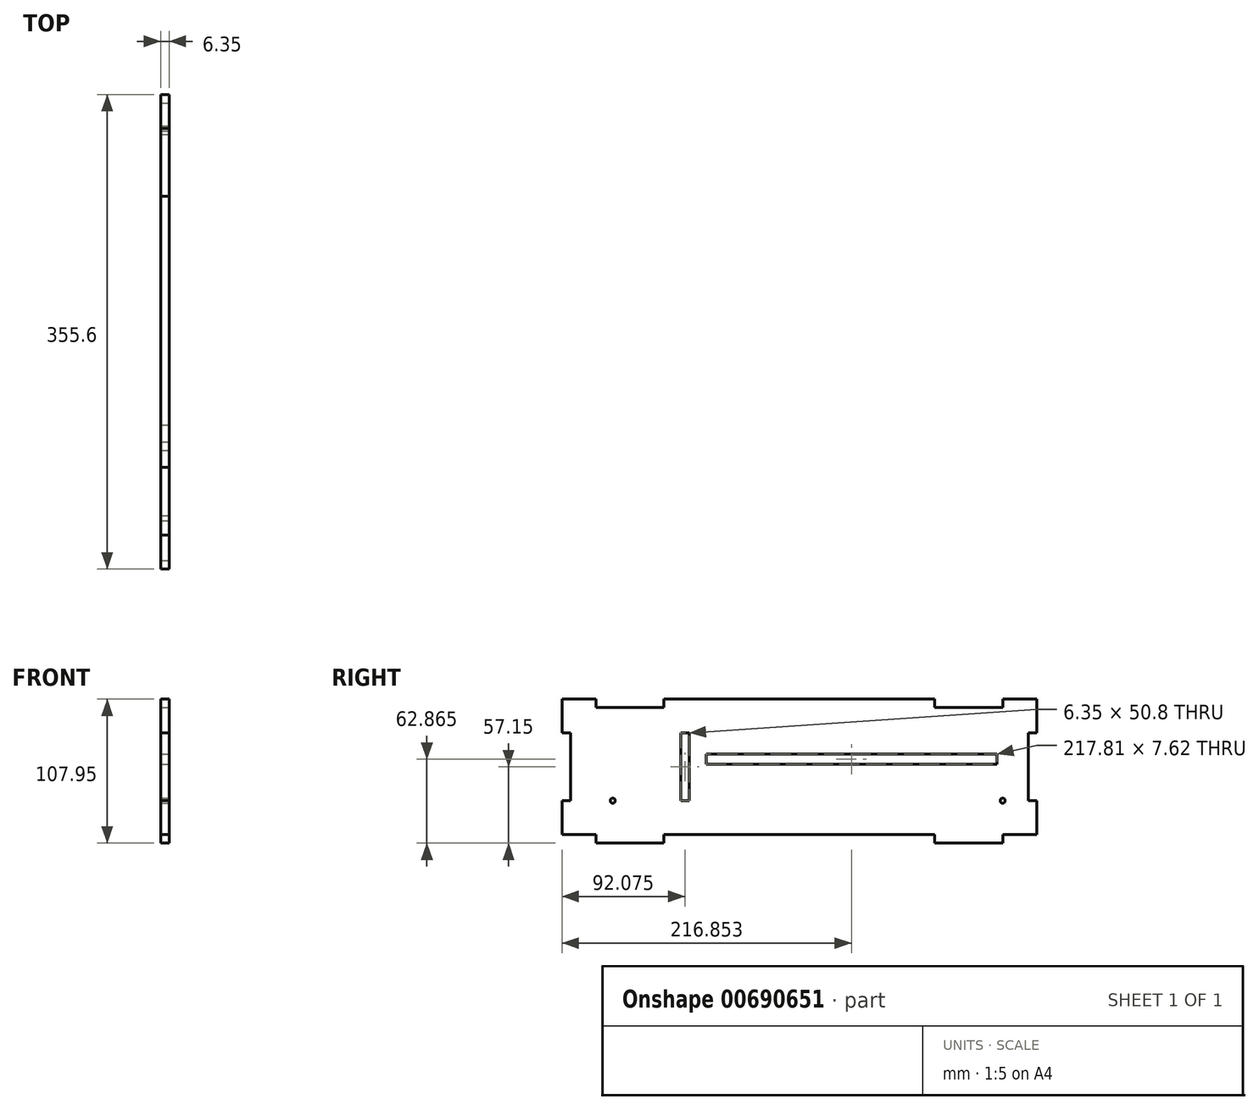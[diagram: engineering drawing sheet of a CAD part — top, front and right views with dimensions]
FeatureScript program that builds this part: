
annotation { "Feature Type Name" : "Feature", "Feature Type Description" : "" }
export const myFeature = defineFeature(function(context is Context, id is Id, definition is map)
    precondition{}
    {
        {
            var Q0;
            Q0=qCreatedBy(makeId("Right.planeOp"),FACE);
            var sketch = newSketch(context, id + "F0", { "sketchPlane" : qUnion([Q0])});
            skLineSegment(sketch, "E0.bottom", {"start": v(-177.8, 101.6) * mm, "end": v(177.8, 101.6) * mm});
            skLineSegment(sketch, "E0.top", {"start": v(-177.8, 0) * mm, "end": v(177.8, 0) * mm});
            skLineSegment(sketch, "E0.left", {"start": v(-177.8, 101.6) * mm, "end": v(-177.8, 0) * mm});
            skLineSegment(sketch, "E0.right", {"start": v(177.8, 101.6) * mm, "end": v(177.8, 0) * mm});
            skSolve(sketch);
        }
        {
            var Q0;
            Q0 = qSketchRegion(id + "F0", true);
            extrude(context, id + "F1", {"entities" : qUnion([Q0]), "depth" : 6.35 * mm, "offsetDistance" : 25.4 * mm});
        }
        {
            var Q0;
            Q0=makeQuery(id+"F1.opExtrude","CAP_FACE",FACE,{"disambiguationData":[OSD([sQuery(id+"F0.wireOp",EDGE,"E0.bottom"),sQuery(id+"F0.wireOp",EDGE,"E0.top"),sQuery(id+"F0.wireOp",EDGE,"E0.left"),sQuery(id+"F0.wireOp",EDGE,"E0.right")])],"isStart":false});
            var sketch = newSketch(context, id + "F2", { "sketchPlane" : qUnion([Q0])});
            skLineSegment(sketch, "E1.bottom", {"start": v(152.4, 0) * mm, "end": v(101.6, 0) * mm});
            skLineSegment(sketch, "E1.top", {"start": v(152.4, -6.35) * mm, "end": v(101.6, -6.35) * mm});
            skLineSegment(sketch, "E1.left", {"start": v(152.4, 0) * mm, "end": v(152.4, -6.35) * mm});
            skLineSegment(sketch, "E1.right", {"start": v(101.6, 0) * mm, "end": v(101.6, -6.35) * mm});
            skLineSegment(sketch, "E2.MirrorCS", {"start": v(-101.6, 0) * mm, "end": v(-101.6, -6.35) * mm});
            skLineSegment(sketch, "E3.MirrorCS", {"start": v(-152.4, 0) * mm, "end": v(-152.4, -6.35) * mm});
            skLineSegment(sketch, "E4.MirrorCS", {"start": v(-152.4, 0) * mm, "end": v(-101.6, 0) * mm});
            skLineSegment(sketch, "E5.MirrorCS", {"start": v(-152.4, -6.35) * mm, "end": v(-101.6, -6.35) * mm});
            skSolve(sketch);
        }
        {
            var Q0;
            Q0 = qSketchRegion(id + "F2", true);
            extrude(context, id + "F3", {"entities" : qUnion([Q0]), "oppositeDirection" : true, "depth" : 6.35 * mm, "offsetDistance" : 25.4 * mm});
        }
        {
            var Q0;
            Q0=makeQuery(id+"F1.opExtrude","CAP_FACE",FACE,{"disambiguationData":[OSD([sQuery(id+"F0.wireOp",EDGE,"E0.bottom"),sQuery(id+"F0.wireOp",EDGE,"E0.top"),sQuery(id+"F0.wireOp",EDGE,"E0.left"),sQuery(id+"F0.wireOp",EDGE,"E0.right")])],"isStart":false});
            var sketch = newSketch(context, id + "F4", { "sketchPlane" : qUnion([Q0])});
            skLineSegment(sketch, "E6", {"start": v(152.4, 0) * mm, "end": v(152.4, 25.4) * mm, "construction": true});
            skLineSegment(sketch, "E7", {"start": v(152.4, 25.4) * mm, "end": v(177.8, 25.4) * mm, "construction": true});
            skCircle(sketch, "E8", {"center": v(152.4, 25.4) * mm, "radius": 1.9 * mm});
            skLineSegment(sketch, "E9", {"start": v(-139.7, 0) * mm, "end": v(-139.7, 25.4) * mm, "construction": true});
            skLineSegment(sketch, "E10", {"start": v(-139.7, 25.4) * mm, "end": v(-177.8, 25.4) * mm, "construction": true});
            skCircle(sketch, "E11", {"center": v(-139.7, 25.4) * mm, "radius": 1.9 * mm});
            skSolve(sketch);
        }
        {
            var Q0;
            Q0 = qSketchRegion(id + "F4", true);
            extrude(context, id + "F5", {"entities" : qUnion([Q0]), "operationType" : NewBodyOperationType.REMOVE, "endBound" : BoundingType.THROUGH_ALL, "oppositeDirection" : true, "depth" : 25.4 * mm, "offsetDistance" : 25.4 * mm});
        }
        {
            var Q0;
            Q0=makeQuery(id+"F1.opExtrude","CAP_FACE",FACE,{"disambiguationData":[OSD([sQuery(id+"F0.wireOp",EDGE,"E0.bottom"),sQuery(id+"F0.wireOp",EDGE,"E0.top"),sQuery(id+"F0.wireOp",EDGE,"E0.left"),sQuery(id+"F0.wireOp",EDGE,"E0.right")])],"isStart":false});
            var sketch = newSketch(context, id + "F6", { "sketchPlane" : qUnion([Q0])});
            skLineSegment(sketch, "E12.bottom", {"start": v(177.8, 76.2) * mm, "end": v(171.45, 76.2) * mm});
            skLineSegment(sketch, "E12.top", {"start": v(177.8, 25.4) * mm, "end": v(171.45, 25.4) * mm});
            skLineSegment(sketch, "E12.left", {"start": v(177.8, 76.2) * mm, "end": v(177.8, 25.4) * mm});
            skLineSegment(sketch, "E12.right", {"start": v(171.45, 76.2) * mm, "end": v(171.45, 25.4) * mm});
            skLineSegment(sketch, "E13.MirrorCS", {"start": v(-177.8, 76.2) * mm, "end": v(-171.45, 76.2) * mm});
            skLineSegment(sketch, "E14.MirrorCS", {"start": v(-177.8, 25.4) * mm, "end": v(-171.45, 25.4) * mm});
            skLineSegment(sketch, "E15.MirrorCS", {"start": v(-177.8, 76.2) * mm, "end": v(-177.8, 25.4) * mm});
            skLineSegment(sketch, "E16.MirrorCS", {"start": v(-171.45, 76.2) * mm, "end": v(-171.45, 25.4) * mm});
            skSolve(sketch);
        }
        {
            var Q0;
            Q0 = qSketchRegion(id + "F6", true);
            extrude(context, id + "F7", {"entities" : qUnion([Q0]), "operationType" : NewBodyOperationType.REMOVE, "oppositeDirection" : true, "depth" : 25.4 * mm, "offsetDistance" : 25.4 * mm});
        }
        {
            var Q0;
            Q0=makeQuery(id+"F3.opExtrude","SWEPT_BODY",BODY,{"disambiguationData":[OSD([sQuery(id+"F2.wireOp",EDGE,"E2.MirrorCS"),sQuery(id+"F2.wireOp",EDGE,"E3.MirrorCS"),sQuery(id+"F2.wireOp",EDGE,"E4.MirrorCS"),sQuery(id+"F2.wireOp",EDGE,"E5.MirrorCS")])]});
            var Q1;
            Q1=makeQuery(id+"F1.opExtrude","SWEPT_BODY",BODY,{"disambiguationData":[OSD([sQuery(id+"F0.wireOp",EDGE,"E0.bottom"),sQuery(id+"F0.wireOp",EDGE,"E0.top"),sQuery(id+"F0.wireOp",EDGE,"E0.left"),sQuery(id+"F0.wireOp",EDGE,"E0.right")])]});
            var Q2;
            Q2=makeQuery(id+"F3.opExtrude","SWEPT_BODY",BODY,{"disambiguationData":[OSD([sQuery(id+"F2.wireOp",EDGE,"E1.bottom"),sQuery(id+"F2.wireOp",EDGE,"E1.top"),sQuery(id+"F2.wireOp",EDGE,"E1.left"),sQuery(id+"F2.wireOp",EDGE,"E1.right")])]});
            booleanBodies(context, id + "F8", {"operationType" : BooleanOperationType.UNION, "tools" : qUnion([Q0, Q1, Q2])});
        }
        {
            var Q0;
            Q0=makeQuery(id+"F8.opBoolean","MERGE",FACE,{"derivedFrom":[makeQuery(id+"F3.opExtrude","CAP_FACE",FACE,{"disambiguationData":[OSD([sQuery(id+"F2.wireOp",EDGE,"E1.bottom"),sQuery(id+"F2.wireOp",EDGE,"E1.top"),sQuery(id+"F2.wireOp",EDGE,"E1.left"),sQuery(id+"F2.wireOp",EDGE,"E1.right")])],"isStart":true}),makeQuery(id+"F3.opExtrude","CAP_FACE",FACE,{"disambiguationData":[OSD([sQuery(id+"F2.wireOp",EDGE,"E2.MirrorCS"),sQuery(id+"F2.wireOp",EDGE,"E3.MirrorCS"),sQuery(id+"F2.wireOp",EDGE,"E4.MirrorCS"),sQuery(id+"F2.wireOp",EDGE,"E5.MirrorCS")])],"isStart":true}),makeQuery(id+"F1.opExtrude","CAP_FACE",FACE,{"disambiguationData":[OSD([sQuery(id+"F0.wireOp",EDGE,"E0.bottom"),sQuery(id+"F0.wireOp",EDGE,"E0.top"),sQuery(id+"F0.wireOp",EDGE,"E0.left"),sQuery(id+"F0.wireOp",EDGE,"E0.right")])],"isStart":false})]});
            var sketch = newSketch(context, id + "F9", { "sketchPlane" : qUnion([Q0])});
            skLineSegment(sketch, "E17.bottom", {"start": v(-88.9, 76.2) * mm, "end": v(-82.55, 76.2) * mm});
            skLineSegment(sketch, "E17.top", {"start": v(-88.9, 25.4) * mm, "end": v(-82.55, 25.4) * mm});
            skLineSegment(sketch, "E17.left", {"start": v(-88.9, 76.2) * mm, "end": v(-88.9, 25.4) * mm});
            skLineSegment(sketch, "E17.right", {"start": v(-82.55, 76.2) * mm, "end": v(-82.55, 25.4) * mm});
            skSolve(sketch);
        }
        {
            var Q0;
            Q0 = qSketchRegion(id + "F9", true);
            extrude(context, id + "F10", {"entities" : qUnion([Q0]), "operationType" : NewBodyOperationType.REMOVE, "oppositeDirection" : true, "depth" : 25.4 * mm, "offsetDistance" : 25.4 * mm});
        }
        {
            var Q0;
            Q0=makeQuery(id+"F8.opBoolean","MERGE",FACE,{"derivedFrom":[makeQuery(id+"F3.opExtrude","CAP_FACE",FACE,{"disambiguationData":[OSD([sQuery(id+"F2.wireOp",EDGE,"E1.bottom"),sQuery(id+"F2.wireOp",EDGE,"E1.top"),sQuery(id+"F2.wireOp",EDGE,"E1.left"),sQuery(id+"F2.wireOp",EDGE,"E1.right")])],"isStart":true}),makeQuery(id+"F3.opExtrude","CAP_FACE",FACE,{"disambiguationData":[OSD([sQuery(id+"F2.wireOp",EDGE,"E2.MirrorCS"),sQuery(id+"F2.wireOp",EDGE,"E3.MirrorCS"),sQuery(id+"F2.wireOp",EDGE,"E4.MirrorCS"),sQuery(id+"F2.wireOp",EDGE,"E5.MirrorCS")])],"isStart":true}),makeQuery(id+"F1.opExtrude","CAP_FACE",FACE,{"disambiguationData":[OSD([sQuery(id+"F0.wireOp",EDGE,"E0.bottom"),sQuery(id+"F0.wireOp",EDGE,"E0.top"),sQuery(id+"F0.wireOp",EDGE,"E0.left"),sQuery(id+"F0.wireOp",EDGE,"E0.right")])],"isStart":false})]});
            var sketch = newSketch(context, id + "F11", { "sketchPlane" : qUnion([Q0])});
            skLineSegment(sketch, "E18.bottom", {"start": v(-152.4, 101.6) * mm, "end": v(-101.6, 101.6) * mm});
            skLineSegment(sketch, "E18.top", {"start": v(-152.4, 95.25) * mm, "end": v(-101.6, 95.25) * mm});
            skLineSegment(sketch, "E18.left", {"start": v(-152.4, 101.6) * mm, "end": v(-152.4, 95.25) * mm});
            skLineSegment(sketch, "E18.right", {"start": v(-101.6, 101.6) * mm, "end": v(-101.6, 95.25) * mm});
            skLineSegment(sketch, "E19.MirrorCS", {"start": v(101.6, 101.6) * mm, "end": v(101.6, 95.25) * mm});
            skLineSegment(sketch, "E20.MirrorCS", {"start": v(152.4, 101.6) * mm, "end": v(152.4, 95.25) * mm});
            skLineSegment(sketch, "E21.MirrorCS", {"start": v(152.4, 95.25) * mm, "end": v(101.6, 95.25) * mm});
            skLineSegment(sketch, "E22.MirrorCS", {"start": v(152.4, 101.6) * mm, "end": v(101.6, 101.6) * mm});
            skSolve(sketch);
        }
        {
            var Q0;
            Q0 = qSketchRegion(id + "F11", true);
            extrude(context, id + "F12", {"entities" : qUnion([Q0]), "operationType" : NewBodyOperationType.REMOVE, "oppositeDirection" : true, "depth" : 25.4 * mm, "offsetDistance" : 25.4 * mm});
        }
        {
            var Q0;
            Q0=makeQuery(id+"F8.opBoolean","MERGE",FACE,{"derivedFrom":[makeQuery(id+"F3.opExtrude","CAP_FACE",FACE,{"disambiguationData":[OSD([sQuery(id+"F2.wireOp",EDGE,"E1.bottom"),sQuery(id+"F2.wireOp",EDGE,"E1.top"),sQuery(id+"F2.wireOp",EDGE,"E1.left"),sQuery(id+"F2.wireOp",EDGE,"E1.right")])],"isStart":true}),makeQuery(id+"F3.opExtrude","CAP_FACE",FACE,{"disambiguationData":[OSD([sQuery(id+"F2.wireOp",EDGE,"E2.MirrorCS"),sQuery(id+"F2.wireOp",EDGE,"E3.MirrorCS"),sQuery(id+"F2.wireOp",EDGE,"E4.MirrorCS"),sQuery(id+"F2.wireOp",EDGE,"E5.MirrorCS")])],"isStart":true}),makeQuery(id+"F1.opExtrude","CAP_FACE",FACE,{"disambiguationData":[OSD([sQuery(id+"F0.wireOp",EDGE,"E0.bottom"),sQuery(id+"F0.wireOp",EDGE,"E0.top"),sQuery(id+"F0.wireOp",EDGE,"E0.left"),sQuery(id+"F0.wireOp",EDGE,"E0.right")])],"isStart":false})]});
            var sketch = newSketch(context, id + "F13", { "sketchPlane" : qUnion([Q0])});
            skLineSegment(sketch, "E23.bottom", {"start": v(-69.85, 60.32) * mm, "end": v(147.96, 60.33) * mm});
            skLineSegment(sketch, "E23.top", {"start": v(-69.85, 52.7) * mm, "end": v(147.96, 52.7) * mm});
            skLineSegment(sketch, "E23.left", {"start": v(-69.85, 60.32) * mm, "end": v(-69.85, 52.7) * mm});
            skLineSegment(sketch, "E23.right", {"start": v(147.96, 60.33) * mm, "end": v(147.96, 52.7) * mm});
            skSolve(sketch);
        }
        {
            var Q0;
            Q0 = qSketchRegion(id + "F13", true);
            extrude(context, id + "F14", {"entities" : qUnion([Q0]), "operationType" : NewBodyOperationType.REMOVE, "oppositeDirection" : true, "depth" : 25.4 * mm, "offsetDistance" : 25.4 * mm});
        }
    });
